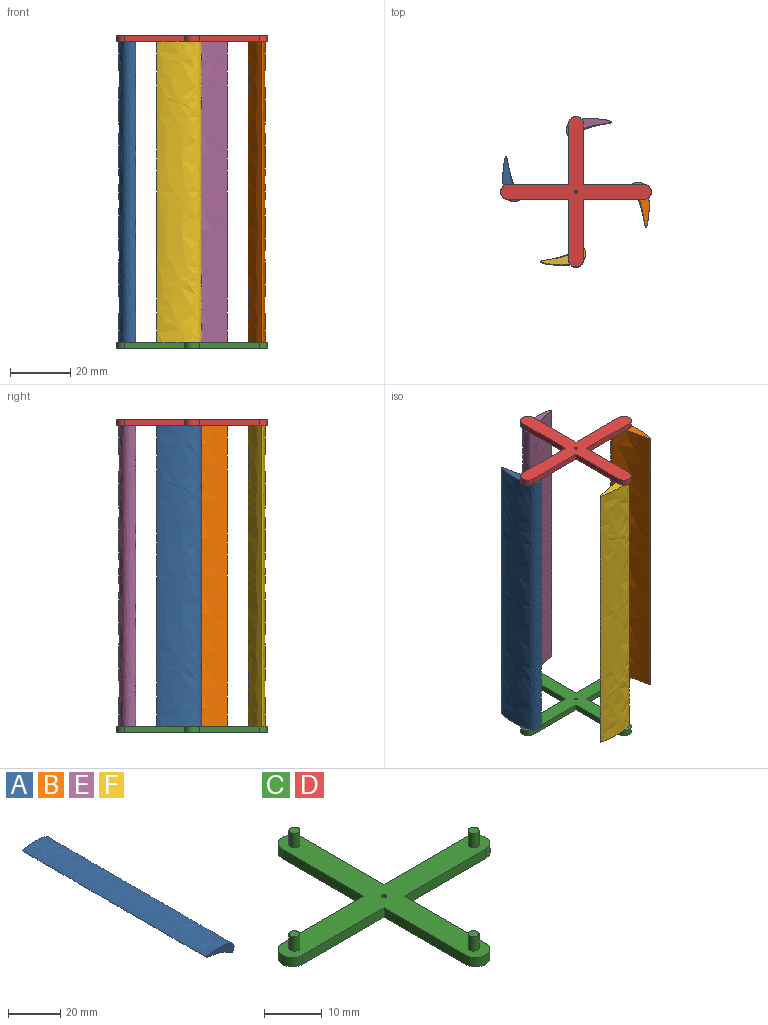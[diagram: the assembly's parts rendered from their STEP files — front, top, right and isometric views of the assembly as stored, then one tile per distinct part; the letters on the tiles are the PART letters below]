
ASSEMBLY  parts=6 mates=5
PART A: 4 faces, bbox 16.3x100x7.3 mm
  f0: extruded ~100x14.96mm, area 3417mm2, adj f2,f3
  f1: cylinder r=1mm len=100mm, axis (0,1,0), area 628.3mm2, adj f2,f3
  f2: plane 16.31x7.27mm, normal (0,-1,0), area 36.4mm2, adj f0,f1
  f3: plane 16.31x7.27mm, normal (0,1,0), area 36.4mm2, adj f0,f1
PART B: same geometry as A
PART C: 23 faces, bbox 50x50x5 mm
  f0: plane 20x2mm, normal (0,1,0), area 40mm2, adj f1,f9,f10,f19
  f1: plane 20x2mm, normal (1,0,0), area 40mm2, adj f0,f9,f10,f22
  f2: plane 20x2mm, normal (-1,0,0), area 40mm2, adj f3,f9,f10,f22
  f3: plane 20x2mm, normal (0,1,0), area 40mm2, adj f2,f9,f10,f21
  f4: plane 20x2mm, normal (0,-1,0), area 40mm2, adj f5,f9,f10,f21
  f5: plane 20x2mm, normal (-1,0,0), area 40mm2, adj f4,f9,f10,f20
  f6: plane 20x2mm, normal (1,0,0), area 40mm2, adj f7,f9,f10,f20
  f7: plane 20x2mm, normal (0,-1,0), area 40mm2, adj f6,f9,f10,f19
  f8: cylinder r=0.5mm len=2mm, axis (0,0,-1), area 6.3mm2, adj f9,f10
  f9: plane 50x50mm, normal (0,0,1), area 452.1mm2, adj f0,f1,f2,f3,f4,f5,f6,f7
  f10: plane 50x50mm, normal (0,0,-1), area 463.5mm2, adj f0,f1,f2,f3,f4,f5,f6,f7
  f11: cylinder r=0.95mm len=3mm, axis (0,0,-1), area 17.9mm2, adj f9,f12
  f12: plane 1.9x1.9mm, normal (0,0,1), area 2.8mm2, adj f11
  f13: cylinder r=0.95mm len=3mm, axis (0,0,-1), area 17.9mm2, adj f9,f14
  f14: plane 1.9x1.9mm, normal (0,0,1), area 2.8mm2, adj f13
  f15: cylinder r=0.95mm len=3mm, axis (0,0,-1), area 17.9mm2, adj f9,f16
  f16: plane 1.9x1.9mm, normal (0,0,1), area 2.8mm2, adj f15
  f17: cylinder r=0.95mm len=3mm, axis (0,0,-1), area 17.9mm2, adj f9,f18
  f18: plane 1.9x1.9mm, normal (0,0,1), area 2.8mm2, adj f17
  f19: cylinder r=2.5mm len=5mm, axis (0,0,-1), area 15.7mm2, adj f0,f7,f9,f10
  f20: cylinder r=2.5mm len=5mm, axis (0,0,-1), area 15.7mm2, adj f5,f6,f9,f10
  f21: cylinder r=2.5mm len=5mm, axis (0,0,1), area 15.7mm2, adj f3,f4,f9,f10
  f22: cylinder r=2.5mm len=5mm, axis (0,0,-1), area 15.7mm2, adj f1,f2,f9,f10
PART D: same geometry as C
PART E: same geometry as A
PART F: same geometry as A
PLACE A rot(axis=(0.58,-0.58,-0.58),120deg) t=(0.88,-23.32,53.89)mm
PLACE B rot(axis=(0.58,0.58,0.58),120deg) t=(5.57,84.51,53.89)mm
PLACE C t=(41.47,1.5,-48.11)mm
PLACE D rot(axis=(1,0,0),180deg) t=(41.47,59.69,55.89)mm
PLACE E rot(axis=(0,-0.71,-0.71),180deg) t=(-50.69,32.94,53.89)mm
PLACE F rot(axis=(1,0,0),90deg) t=(57.14,28.25,53.89)mm
MATE slider A.f1 <-> C.f11  axis (0,0,-1) through (-18.78,30.6,-46.11)mm
MATE slider E.f1 <-> C.f13  axis (0,0,-1) through (3.22,52.6,-46.11)mm
MATE slider D.f11 <-> A.f1  axis (0,0,-1) through (-18.78,30.6,53.89)mm
MATE slider B.f1 <-> C.f15  axis (0,0,-1) through (25.22,30.6,-46.11)mm
MATE slider F.f1 <-> C.f17  axis (0,0,-1) through (3.22,8.6,-46.11)mm
